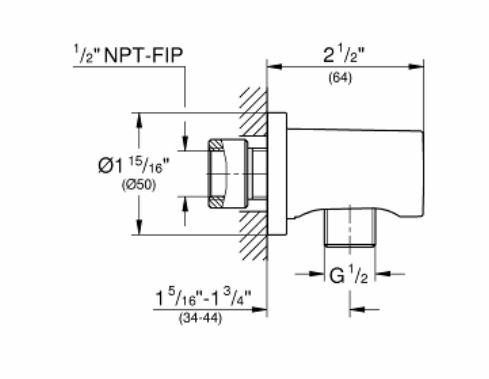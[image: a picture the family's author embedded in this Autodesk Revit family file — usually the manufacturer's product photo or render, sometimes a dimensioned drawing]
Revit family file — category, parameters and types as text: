
# Revit family: Commercial_Shower_System-GROHE-Timeless-29430_Series
name_source: partatom
category: Plumbing Fixtures
units: mm (PartAtom-declared; Revit-internal decimal feet)

## family parameters
Cut with Voids When Loaded = No
Host = Face
OmniClass Number = 23.45.05.14.17
OmniClass Title = Showers
Part Type = Normal
Room Calculation Point = No
Round Connector Dimension = Use Diameter
Shared = Yes

## types (4) — shared parameters
26 569- Rainshower™ 310 Mono showerhead, 1 spray, 1.75gpm = Yes
26 602- Rainshower™ 24” Shower Bar = Yes
26 635- Rainshower™ wall union = Yes
26 866- Includes Sena Hand Shower, 1 spray, 1.75gpm = Yes
28 417- RotaFlex Metal Longlife metallic hose = Yes
28 540- Rainshower™ 15” shower arm = Yes
29 423- Timeless Pressure Balance Valve Trim with 2-Way Diverter = Yes
35 117- GrohSafe™ 3.0 Pressure Balance Rough Valve with Integrated Diverter = Yes
ASME A112.18.1/CSA B125.1/ASSE 1016 = Yes
ASSE 1016 = Yes
Assembly Code = D2010710
CEC Compliant = Yes
CW Connection = Yes
CWFU = 3
CalGreen Compliant = Yes
Cold Water Connection Description = 1/2" NPT Female CW Inlet Connection
Cold Water Connection Diameter = 1/2"
Connection Diameter = 1/2"
Default Elevation = 0"
Description = TIMELESS- Pressure Balance Rainshower Set
Double check valves = Included
EPA WaterSense® Certified = Yes
Flow Rate = Max. 1.75gpm (6.6L/min)
HW Connection = Yes
HWFU = 3
Height- Diverter = 48"
Height- Showerhead = 78"
Hot Water Connection Description = 1/2" NPT Female HW Inlet Connection
Hot Water Connection Diameter = 1/2"
IAPMO Compliance = Massachusetts Plumbing Board Approved, Energy Policy Act of 1992, CSA B125.16
Installation Type = Wall Mounted
Manufacturer = GROHE
Price = Prices may vary. Please consult Manufacturer Representative for most up-to-date price list.
Tempered Water Connection = Yes
URL = https://www.grohe.us
Vent Connection = No
WFU = 4
Waste Connection = No

## per-type parameters (varying)
| type | Finish | Material |
| 29430000 | Metal-Grohe-000-StarLight Chrome | Metal-Grohe-000-StarLight Chrome |
| 29430A00 | Metal-Grohe-A00-Hard Graphite | Metal-Grohe-A00-Hard Graphite |
| 29430EN0 | Metal-Grohe-EN0-Brushed Nickel Infinity Finish | Metal-Grohe-EN0-Brushed Nickel Infinity Finish |
| 29430GN0 | Metal-Grohe-GN0-Brushed Cool Sunrise | Metal-Grohe-GN0-Brushed Cool Sunrise |

note: column(s) folded — value = type name in every type: Model

## geometry (parser evidence)
native form markers: Sweep x16
no freeform markers — native parametric forms only
